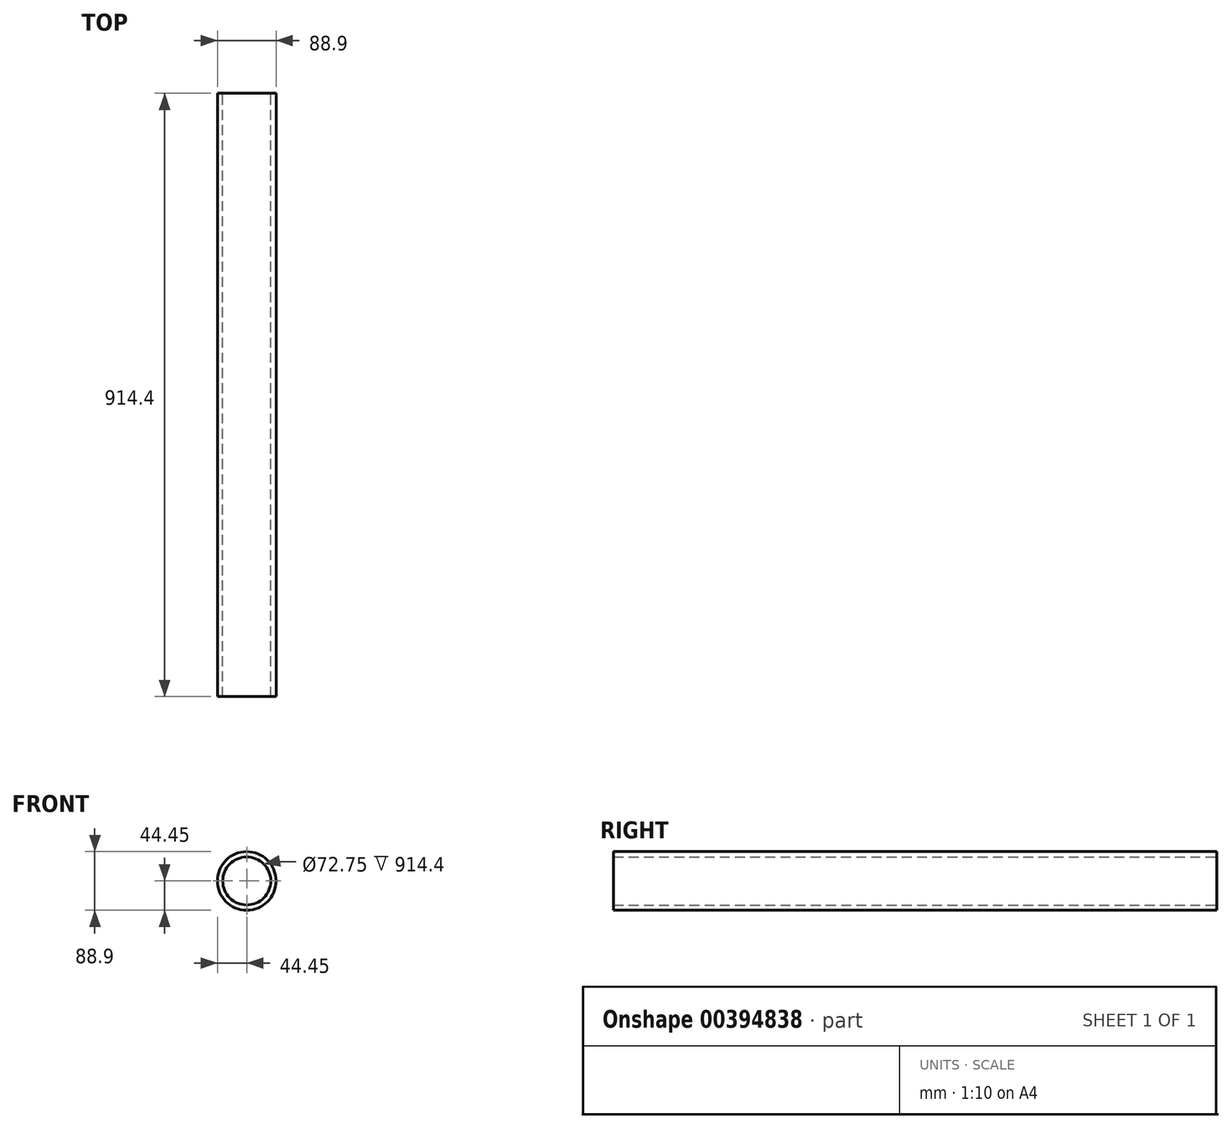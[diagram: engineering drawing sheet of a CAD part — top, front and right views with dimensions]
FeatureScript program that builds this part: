
annotation { "Feature Type Name" : "Feature", "Feature Type Description" : "" }
export const myFeature = defineFeature(function(context is Context, id is Id, definition is map)
    precondition{}
    {
        {
            var Q0;
            Q0=qCreatedBy(makeId("Front.planeOp"),FACE);
            var sketch = newSketch(context, id + "F0", { "sketchPlane" : qUnion([Q0])});
            skCircle(sketch, "E0", {"center": v(0, 0) * mm, "radius": 44.45 * mm});
            skCircle(sketch, "E1", {"center": v(0, 0) * mm, "radius": 36.37 * mm});
            skSolve(sketch);
        }
        {
            var Q0;
            Q0=qSketchRegion(id+"F0",true);
            extrude(context, id + "F1", {"entities" : qUnion([Q0]), "depth" : 914.4 * mm});
        }
    });
